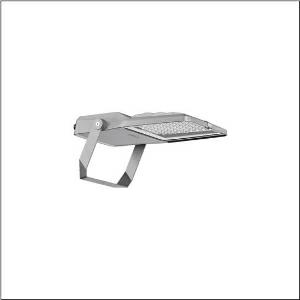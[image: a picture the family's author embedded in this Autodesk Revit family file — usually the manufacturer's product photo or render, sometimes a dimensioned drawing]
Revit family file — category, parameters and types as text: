
# Revit family: floodlight_fl_21_iq_mini___pl33t_5xa7772b3f1a_8999
name_source: partatom
category: Lighting Fixtures
units: mm (PartAtom-declared; Revit-internal decimal feet)

## family parameters
Cut with Voids When Loaded = No
Host = Face
Light Source = No
Part Type = Normal
Room Calculation Point = No
Round Connector Dimension = Use Diameter
Shared = No

## types (1)
- --- (1 x LED, 5310 lm, 45.5 W, 3000K)
    Apparent Load = 46 VA
    CIE Flux Codes = 26 75 99 100 100
    Color Rendering = 80
    Color Temperature = 3000K
    Default Elevation = 1800 mm
    Description = Floodlight FL 21 iQ mini, floodlight, primary light control with lens, of PMMA, primary optical cover: protective disc, of toughened safety glass, transparent, light distribution: PL33T, light emission: direct distribution, installation type: surface-mounted, LED, High Power LED, rated luminous flux: 5.310lm, luminous efficacy: 117lm/W, light colour: 830, colour temperature: 3000K, control gear: iQ Street-Remote/DALI, control: Street-Remote, Auto-Match, Temp-Guard, Night-Set, Smart-Wire, Desk-Remote (wireless, voltage-free reading and setting of iQ features in the workshop via application-optimized NFC function/RFID function), optimised constant luminous flux control (CLO 2.0), with terminal, 6-pole, mains connection: 220..240V, AC, 50/60Hz, start of lifetime: 46W, end of service life: 48W, reduction: 21W, luminaire housing, of diecast aluminium, powder-coated, Siteco® metallic grey (DB 702S), corrosivity category C5 mid according to DIN EN ISO 12944, suitable for swimming pools, chlorine-resistant, sealing non-destructively replaceable, mounting bracket, of steel, galvanised, powder-coated, Siteco® metallic grey (DB 702S), protection rating (complete): IP66, insulation class (complete): insulation class II (safety insulation), certification: CE, ENEC, VDE, protection symbol: D, impact resistance: IK08, permissible operating ambient temperature: -40..+40°C, permissible operating ambient temperature for outdoor applications: -40..+50°C, standard: DIN EN 12944, LABS conformity tested according to VDMA 24364:2018-05, packaging unit: 1 piece

Light Distribution: PL33T
    Height = 70 mm
    Lamp = 1 x LED
    Lamp Light Flux = 5310 lm
    Lamp Power = 45.5 W
    Lamp count = 1
    Length = 485 mm
    Luminous efficacy = 117 lm/W
    Manufacturer = Siteco
    ModVariant = No
    Model = 5XA7772B3F1A
    Number of Poles = 1
    OnlyDefault = Yes
    Power Factor = 1
    Product Name = Floodlight FL 21 iQ mini | PL33T
    Product group = floodlight | pylon annexe
    ProductGroupID = 6200
    Protection Class = Protection class II
    Protection Degree = IP 66
    RLX_Detail_Level = 1
    RLX_Emergency_Light_Flux = 0 lm
    RLX_Emergency_Type = 0
    RLX_Emergency_Type_DB = No
    RlxData = <blob elided: 96201 chars, md5=43185dc9>
    Socket = socket
    Standby Power = 0 W
    System Light Flux = 5310 lm
    System Power = 46 W
    Type Comments = factory setting: luminous flux: 100 % | dim-lin: 254 | 463 mA
    Type Image = l_1006845.jpg
    URL = http://relux.com
    VarID = @adj_149996
    Voltage = 0 V
    Weight = 0.00 kg
    Width = 337 mm

## geometry (parser evidence)
native form markers: Blend x4, Sweep x12
no freeform markers — native parametric forms only
